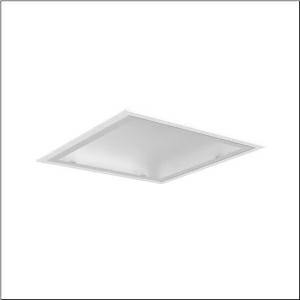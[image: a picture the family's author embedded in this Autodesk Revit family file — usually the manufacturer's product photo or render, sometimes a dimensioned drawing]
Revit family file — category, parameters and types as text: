
# Revit family: mira_r__11_51fr127a441a_e192
name_source: partatom
category: Lighting Fixtures
units: mm (PartAtom-declared; Revit-internal decimal feet)

## family parameters
Cut with Voids When Loaded = No
Host = Face
Light Source = No
Part Type = Normal
Room Calculation Point = No
Round Connector Dimension = Use Diameter
Shared = No

## types (1)
- Mira® 11 (1 x LED, 4610 lm, 37 W, 4000K)
    Apparent Load = 37 VA
    CIE Flux Codes = 51 82 97 100 100
    Color Rendering = 80
    Color Temperature = 4000K
    Default Elevation = 1800 mm
    Description = Mira® 11, clean room luminaire, primary light control with reflector, primary optical cover: cover, of toughened safety glass, light emission: direct distribution, primary light characteristic: symmetric, installation type: recessed, LED, rated luminous flux: 4.610lm, luminous efficacy: 125lm/W, light colour: 840, colour temperature: 4000K, control gear: ON/OFF, with terminal, 3-pole, max. 2.5mm², mains connection: 230V, AC, 50/60Hz, rated input power: 37W, luminaire housing, of sheet steel, coated, pure white (RAL 9010), with concealed magnets, module: M625, length: 623mm, width: 623mm, height: 90mm, protection rating (complete): IP65, insulation class (complete): insulation class I (protective earthing), certification: CE, UKCA, permissible operating ambient temperature: -5..+40°C, standard: EN 50419, packaging unit: 1 piece
    Height = 0 mm  [stored 0 ft]
    Lamp = 1 x LED
    Lamp Light Flux = 4610 lm
    Lamp Power = 37 W
    Lamp count = 1
    Length = 625 mm
    Luminous efficacy = 125 lm/W
    Manufacturer = Siteco
    ModVariant = No
    Model = 51FR127A441A
    Mounting Place = Ceiling
    Mounting Type = Recessed
    Number of Poles = 1
    OnlyDefault = Yes
    Power Factor = 1
    Product Name = Mira® 11
    Product group = clean room luminaire | ceiling recessed
    ProductGroupID = 402
    Protection Class = Protection class I
    Protection Degree = IP 65
    RLX_Detail_Level = 1
    RLX_Emergency_Light_Flux = 0 lm
    RLX_Emergency_Type = 0
    RLX_Emergency_Type_DB = No
    RlxData = <blob elided: 19285 chars, md5=2013dbd2>
    Socket = socket
    Standby Power = 0 W
    System Light Flux = 4610 lm
    System Power = 37 W
    Type Comments = Product without accessories
    Type Image = l_1006636.jpg
    URL = http://relux.com
    VarID = ---
    Voltage = 0 V
    Weight = 0.00 kg
    Width = 625 mm

note: [stored X ft] marks values corroborated as IEEE doubles in the binary element streams (Revit-internal decimal feet)

## geometry (parser evidence)
native form markers: Blend x4, Sweep x9
no freeform markers — native parametric forms only
